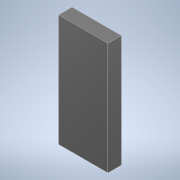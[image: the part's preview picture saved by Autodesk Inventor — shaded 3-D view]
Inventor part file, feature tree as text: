
AUTODESK INVENTOR PART (.ipt)
format: ipt  version: 2022 (Build 260153000, 153)  size: 92,672 bytes
history: native  units: in
note: dims shown in document units (in); Inventor stores cm internally (conversion verified against a paired STEP export)
features: extrude x1, sketch x1
ambient origin geometry x8: Origin, YZ Plane, XZ Plane, XY Plane, X Axis, Y Axis, Z Axis, Center Point
bodies: Solid1 (feature_tree)
feature tree (2):
  extrude  "Extrusion1"  Depth=0.4331in
  sketch  "Sketch1"  dims[d2=0.1181in d3=0.0in d9=0.4331in d10=0.9843in]
